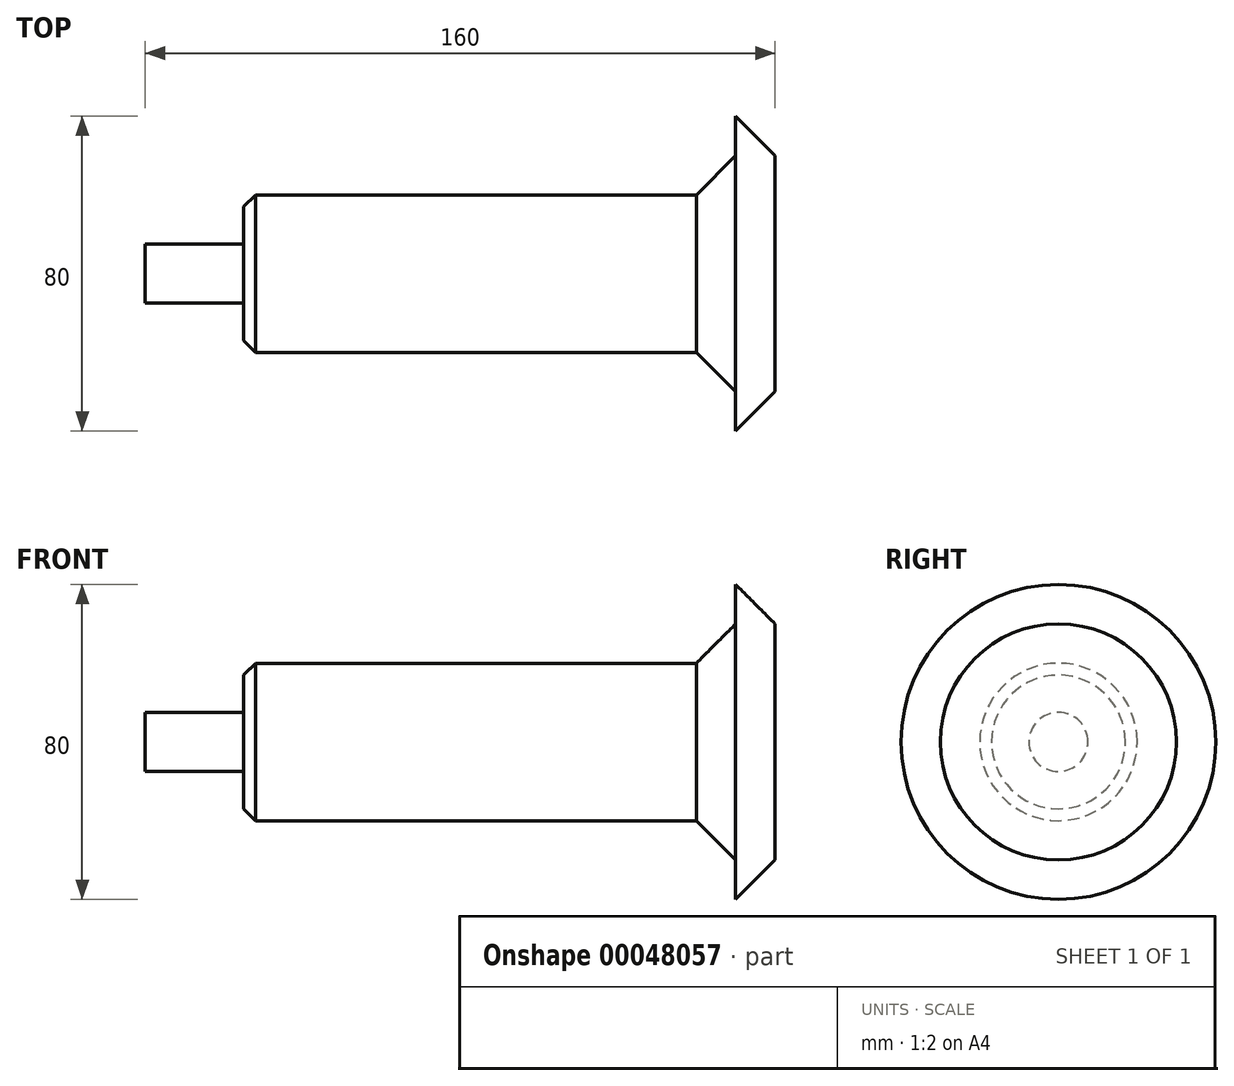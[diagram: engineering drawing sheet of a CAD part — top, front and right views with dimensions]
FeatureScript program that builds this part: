
annotation { "Feature Type Name" : "Feature", "Feature Type Description" : "" }
export const myFeature = defineFeature(function(context is Context, id is Id, definition is map)
    precondition{}
    {
        {
            var Q0;
            Q0=qCreatedBy(makeId("Front.planeOp"),FACE);
            var sketch = newSketch(context, id + "F0", { "sketchPlane" : qUnion([Q0])});
            skLineSegment(sketch, "E0.bottom", {"start": v(0, 0) * mm, "end": v(25, 0) * mm});
            skLineSegment(sketch, "E0.top", {"start": v(0, 15) * mm, "end": v(25, 15) * mm});
            skLineSegment(sketch, "E0.left", {"start": v(0, 0) * mm, "end": v(0, 15) * mm});
            skLineSegment(sketch, "E0.right", {"start": v(25, 0) * mm, "end": v(25, 15) * mm});
            skLineSegment(sketch, "E1.bottom", {"start": v(25, -12.5) * mm, "end": v(140, -12.5) * mm});
            skLineSegment(sketch, "E1.top", {"start": v(25, 27.5) * mm, "end": v(140, 27.5) * mm});
            skLineSegment(sketch, "E1.left", {"start": v(25, -12.5) * mm, "end": v(25, 27.5) * mm});
            skLineSegment(sketch, "E1.right", {"start": v(140, -12.5) * mm, "end": v(140, 27.5) * mm});
            skLineSegment(sketch, "E2.left", {"start": v(140, 27.5) * mm, "end": v(140, -12.5) * mm});
            skLineSegment(sketch, "E2.right", {"start": v(150, 37.5) * mm, "end": v(150, -22.5) * mm});
            skLineSegment(sketch, "E3.bottom", {"start": v(150, -32.5) * mm, "end": v(160, -32.5) * mm});
            skLineSegment(sketch, "E3.top", {"start": v(150, 47.5) * mm, "end": v(160, 47.5) * mm});
            skLineSegment(sketch, "E3.left", {"start": v(150, -32.5) * mm, "end": v(150, 47.5) * mm});
            skLineSegment(sketch, "E3.right", {"start": v(160, -32.5) * mm, "end": v(160, 47.5) * mm});
            skLineSegment(sketch, "E4", {"start": v(0, 7.5) * mm, "end": v(160, 7.5) * mm});
            skPoint(sketch, "E5.orphan", {"position": v(140, 45.95) * mm});
            skLineSegment(sketch, "E6", {"start": v(140, 27.5) * mm, "end": v(150, 37.5) * mm});
            skLineSegment(sketch, "E7", {"start": v(140, -12.5) * mm, "end": v(150, -22.5) * mm});
            skSolve(sketch);
        }
        {
            var Q0;
            {var subQ5=sQuery(id+"F0.wireOp",EDGE,"E0.top");Q0=makeQuery(id+"F0.imprint","IMPRINT",FACE,{"disambiguationData":[TD([[makeQuery(id+"F0.imprint","IMPRINT",EDGE,{"derivedFrom":subQ5}),-1.0]])]});}
            var Q1;
            {var subQ0=sQuery(id+"F0.wireOp",EDGE,"E1.top");Q1=makeQuery(id+"F0.imprint","IMPRINT",FACE,{"disambiguationData":[TD([[makeQuery(id+"F0.imprint","IMPRINT",EDGE,{"derivedFrom":subQ0}),-1.0]])]});}
            var Q2;
            {var subQ5=sQuery(id+"F0.wireOp",EDGE,"E6");Q2=makeQuery(id+"F0.imprint","IMPRINT",FACE,{"disambiguationData":[TD([[makeQuery(id+"F0.imprint","IMPRINT",EDGE,{"derivedFrom":subQ5}),-1.0]])]});}
            var Q3;
            {var subQ6=sQuery(id+"F0.wireOp",EDGE,"E3.top");Q3=makeQuery(id+"F0.imprint","IMPRINT",FACE,{"disambiguationData":[TD([[makeQuery(id+"F0.imprint","IMPRINT",EDGE,{"derivedFrom":subQ6}),-1.0]])]});}
            var Q4;
            Q4=sQuery(id+"F0.wireOp",EDGE,"E4");
            revolve(context, id + "F1", {"entities" : qUnion([Q0, Q1, Q2, Q3]), "axis" : qUnion([Q4]), "revolveType" : RevolveType.FULL});
        }
        {
            var Q0;
            Q0=makeQuery(id+"F1.opRevolve","SWEPT_EDGE",EDGE,{"disambiguationData":[OSD([sQuery(id+"F0.wireOp",EDGE,"E1.top"),sQuery(id+"F0.wireOp",EDGE,"E1.left")])]});
            chamfer(context, id + "F2", {"entities" : qUnion([Q0]), "chamferType" : ChamferType.OFFSET_ANGLE, "width" : 3 * mm, "oppositeDirection" : false, "angle" : 45 * degree, "tangentPropagation" : true});
        }
        {
            var Q0;
            Q0=makeQuery(id+"F1.opRevolve","SWEPT_EDGE",EDGE,{"disambiguationData":[OSD([sQuery(id+"F0.wireOp",EDGE,"E3.top"),sQuery(id+"F0.wireOp",EDGE,"E3.right")])]});
            chamfer(context, id + "F3", {"entities" : qUnion([Q0]), "chamferType" : ChamferType.OFFSET_ANGLE, "width" : 10 * mm, "oppositeDirection" : false, "angle" : 45 * degree, "tangentPropagation" : true});
        }
    });
